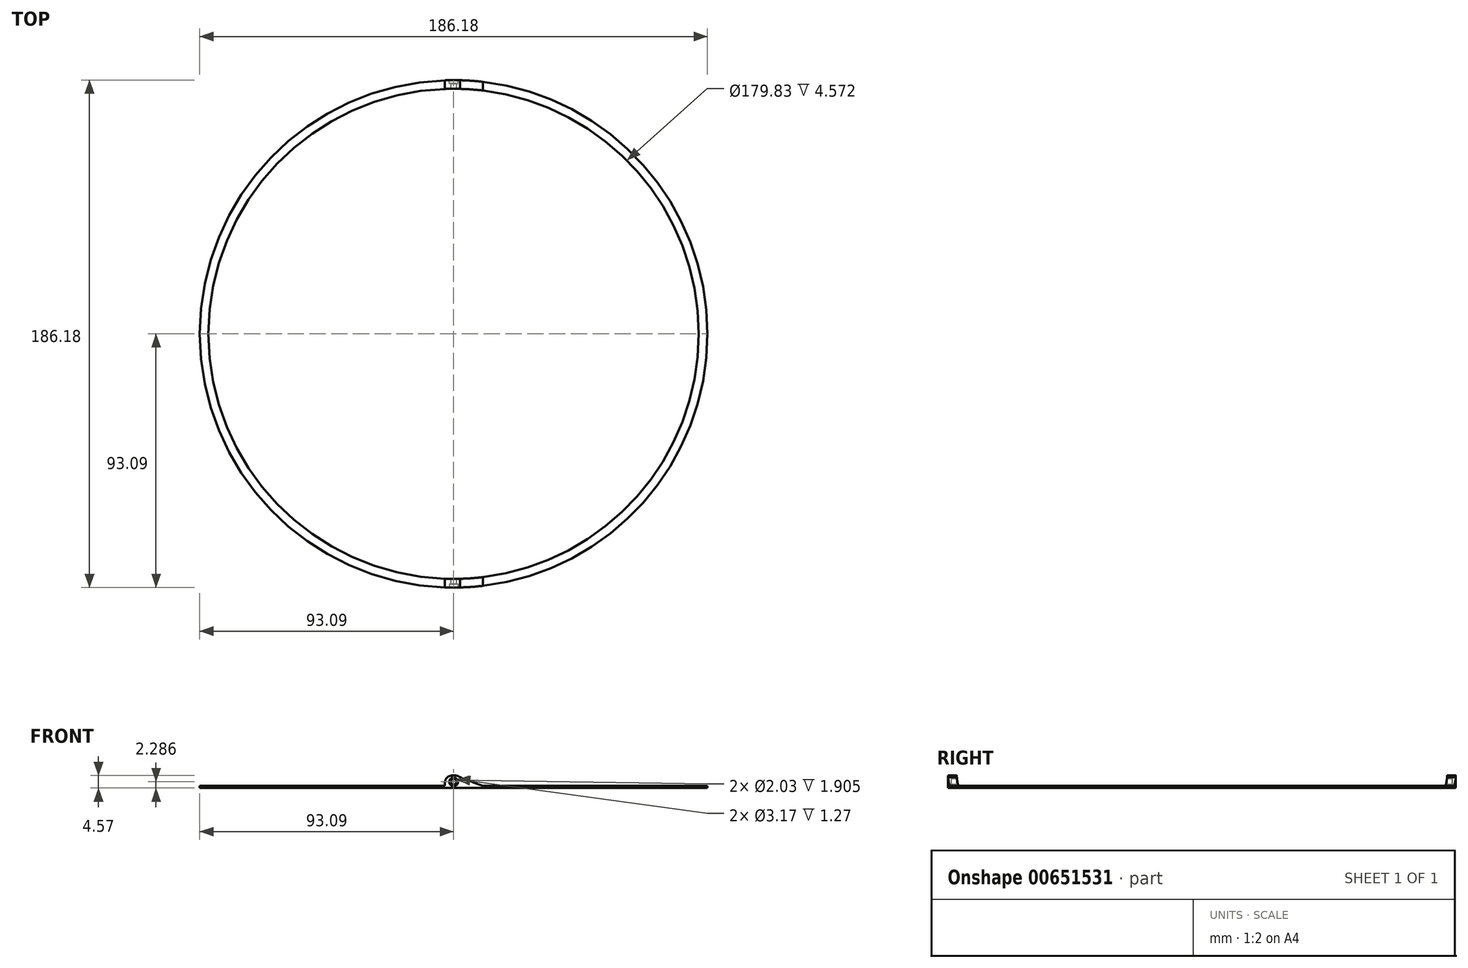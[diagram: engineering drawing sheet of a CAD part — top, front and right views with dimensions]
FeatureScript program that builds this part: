
annotation { "Feature Type Name" : "Feature", "Feature Type Description" : "" }
export const myFeature = defineFeature(function(context is Context, id is Id, definition is map)
    precondition{}
    {
        {
            var Q0;
            Q0=qCreatedBy(makeId("Top.planeOp"),FACE);
            var sketch = newSketch(context, id + "F0", { "sketchPlane" : qUnion([Q0])});
            skCircle(sketch, "E0", {"center": v(0, 0) * mm, "radius": 89.92 * mm});
            skCircle(sketch, "E1", {"center": v(0, 0) * mm, "radius": 93.1 * mm});
            skSolve(sketch);
        }
        {
            var Q0;
            Q0 = qSketchRegion(id + "F0", true);
            extrude(context, id + "F1", {"entities" : qUnion([Q0]), "depth" : 0.76 * mm, "offsetDistance" : 25.4 * mm});
        }
        {
            var Q0;
            Q0=makeQuery(id+"F1.opExtrude","CAP_FACE",FACE,{"disambiguationData":[OSD([sQuery(id+"F0.wireOp",EDGE,"E0"),sQuery(id+"F0.wireOp",EDGE,"E1")])],"isStart":false});
            var sketch = newSketch(context, id + "F2", { "sketchPlane" : qUnion([Q0])});
            skLineSegment(sketch, "E2", {"start": v(-3.18, -89.86) * mm, "end": v(-3.18, -93.04) * mm});
            skLineSegment(sketch, "E3", {"start": v(3.18, -89.86) * mm, "end": v(3.18, -93.04) * mm});
            skArc(sketch, "E4.0", {"start": v(-3.17, -89.86) * mm, "mid": v(0, -89.92) * mm, "end": v(3.17, -89.86) * mm});
            skArc(sketch, "E5.0", {"start": v(-3.18, -93.04) * mm, "mid": v(0, -93.1) * mm, "end": v(3.17, -93.04) * mm});
            skLineSegment(sketch, "E6.MirrorCS", {"start": v(3.18, 89.86) * mm, "end": v(3.18, 93.04) * mm});
            skLineSegment(sketch, "E7.MirrorCS", {"start": v(-3.18, 89.86) * mm, "end": v(-3.18, 93.04) * mm});
            skArc(sketch, "E8.MirrorCS", {"start": v(-3.18, 93.04) * mm, "mid": v(0, 93.1) * mm, "end": v(3.17, 93.04) * mm});
            skArc(sketch, "E9.MirrorCS", {"start": v(-3.17, 89.86) * mm, "mid": v(0, 89.92) * mm, "end": v(3.17, 89.86) * mm});
            skSolve(sketch);
        }
        {
            var Q0;
            Q0 = qSketchRegion(id + "F2", true);
            extrude(context, id + "F3", {"entities" : qUnion([Q0]), "operationType" : NewBodyOperationType.ADD, "depth" : 3.8 * mm, "offsetDistance" : 25.4 * mm});
        }
        {
            var Q0;
            Q0=makeQuery(id+"F3.opExtrude","CAP_EDGE",EDGE,{"disambiguationData":[OSD([sQuery(id+"F2.wireOp",EDGE,"E3")])],"isStart":false});
            var Q1;
            Q1=makeQuery(id+"F3.opExtrude","CAP_EDGE",EDGE,{"disambiguationData":[OSD([sQuery(id+"F2.wireOp",EDGE,"E2")])],"isStart":false});
            var Q2;
            Q2=makeQuery(id+"F3.opExtrude","CAP_EDGE",EDGE,{"disambiguationData":[OSD([sQuery(id+"F2.wireOp",EDGE,"E7.MirrorCS")])],"isStart":false});
            var Q3;
            Q3=makeQuery(id+"F3.opExtrude","CAP_EDGE",EDGE,{"disambiguationData":[OSD([sQuery(id+"F2.wireOp",EDGE,"E6.MirrorCS")])],"isStart":false});
            fillet(context, id + "F4", {"entities" : qUnion([Q0, Q1, Q2, Q3]), "radius" : 2.54 * mm, "tangentPropagation" : true, "allowEdgeOverflow" : false});
        }
        {
            var Q0;
            Q0=makeQuery(id+"F3.opExtrude","CAP_EDGE",EDGE,{"disambiguationData":[OSD([sQuery(id+"F2.wireOp",EDGE,"E7.MirrorCS")])],"isStart":true});
            var Q1;
            Q1=makeQuery(id+"F3.opExtrude","CAP_EDGE",EDGE,{"disambiguationData":[OSD([sQuery(id+"F2.wireOp",EDGE,"E6.MirrorCS")])],"isStart":true});
            var Q2;
            Q2=makeQuery(id+"F3.opExtrude","CAP_EDGE",EDGE,{"disambiguationData":[OSD([sQuery(id+"F2.wireOp",EDGE,"E3")])],"isStart":true});
            var Q3;
            Q3=makeQuery(id+"F3.opExtrude","CAP_EDGE",EDGE,{"disambiguationData":[OSD([sQuery(id+"F2.wireOp",EDGE,"E2")])],"isStart":true});
            chamfer(context, id + "F5", {"entities" : qUnion([Q0, Q1, Q2, Q3]), "width" : 12.7 * mm, "tangentPropagation" : true});
        }
        {
            var Q0;
            Q0=qCreatedBy(makeId("Front.planeOp"),FACE);
            var sketch = newSketch(context, id + "F6", { "sketchPlane" : qUnion([Q0])});
            skCircle(sketch, "E10", {"center": v(0, 2.29) * mm, "radius": 1.02 * mm});
            skSolve(sketch);
        }
        {
            var Q0;
            Q0 = qSketchRegion(id + "F6", true);
            extrude(context, id + "F7", {"entities" : qUnion([Q0]), "operationType" : NewBodyOperationType.REMOVE, "endBound" : BoundingType.SYMMETRIC, "oppositeDirection" : true, "depth" : 508 * mm, "offsetDistance" : 25.4 * mm});
        }
        {
            var Q0;
            Q0=qCreatedBy(makeId("Front.planeOp"),FACE);
            cPlane(context, id + "F8", {"entities" : qUnion([Q0]), "cplaneType" : CPlaneType.OFFSET, "offset" : 93.1 * mm, "width" : 152.4 * mm, "height" : 152.4 * mm});
        }
        {
            var Q0;
            Q0=qCreatedBy(makeId("Front.planeOp"),FACE);
            cPlane(context, id + "F9", {"entities" : qUnion([Q0]), "cplaneType" : CPlaneType.OFFSET, "offset" : 93.1 * mm, "oppositeDirection" : true, "width" : 152.4 * mm, "height" : 152.4 * mm});
        }
        {
            var Q0;
            Q0=qCreatedBy(id+"F8.planeOp",FACE);
            var sketch = newSketch(context, id + "F10", { "sketchPlane" : qUnion([Q0])});
            skCircle(sketch, "E11.0", {"center": v(0, 2.29) * mm, "radius": 1.02 * mm});
            skCircle(sketch, "E12", {"center": v(0, 2.29) * mm, "radius": 1.59 * mm});
            skSolve(sketch);
        }
        {
            var Q0;
            Q0 = qSketchRegion(id + "F10", true);
            extrude(context, id + "F11", {"entities" : qUnion([Q0]), "operationType" : NewBodyOperationType.REMOVE, "oppositeDirection" : true, "depth" : 1.27 * mm, "offsetDistance" : 25.4 * mm});
        }
        {
            var Q0;
            Q0=qCreatedBy(id+"F9.planeOp",FACE);
            var sketch = newSketch(context, id + "F12", { "sketchPlane" : qUnion([Q0])});
            skCircle(sketch, "E13.0", {"center": v(0, 2.29) * mm, "radius": 1.02 * mm});
            skCircle(sketch, "E14", {"center": v(0, 2.29) * mm, "radius": 1.59 * mm});
            skSolve(sketch);
        }
        {
            var Q0;
            Q0=makeQuery(id+"F12.imprint","IMPRINT",FACE,{"disambiguationData":[TD([[makeQuery(id+"F12.imprint","IMPRINT",EDGE,{"derivedFrom":sQuery(id+"F12.wireOp",EDGE,"E13.0")}),-1.0]])]});
            extrude(context, id + "F13", {"entities" : qUnion([Q0]), "operationType" : NewBodyOperationType.REMOVE, "depth" : 1.27 * mm, "offsetDistance" : 25.4 * mm});
        }
    });
